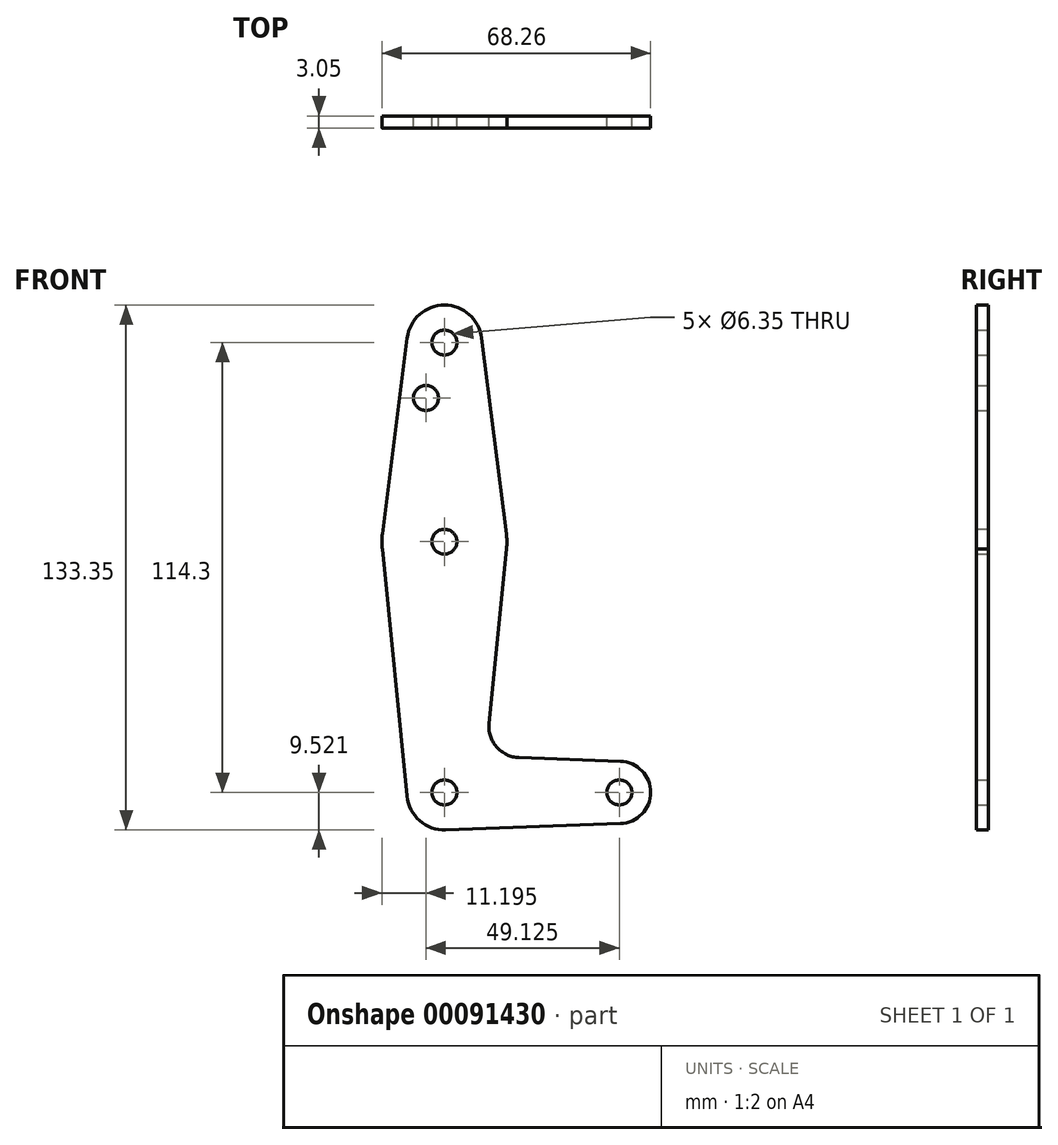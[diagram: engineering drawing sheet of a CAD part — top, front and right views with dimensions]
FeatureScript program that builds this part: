
annotation { "Feature Type Name" : "Feature", "Feature Type Description" : "" }
export const myFeature = defineFeature(function(context is Context, id is Id, definition is map)
    precondition{}
    {
        {
            var Q0;
            Q0=qCreatedBy(makeId("Front.planeOp"),FACE);
            var sketch = newSketch(context, id + "F0", { "sketchPlane" : qUnion([Q0])});
            skLineSegment(sketch, "E0", {"start": v(0, 50.6) * mm, "end": v(0, -63.7) * mm, "construction": true});
            skCircle(sketch, "E1", {"center": v(0, 50.6) * mm, "radius": 9.53 * mm});
            skCircle(sketch, "E2", {"center": v(0, -63.7) * mm, "radius": 9.53 * mm});
            skLineSegment(sketch, "E3", {"start": v(0, -63.7) * mm, "end": v(0, -0.2) * mm, "construction": true});
            skCircle(sketch, "E4", {"center": v(0, 0) * mm, "radius": 15.88 * mm});
            skLineSegment(sketch, "E5", {"start": v(0, -63.7) * mm, "end": v(44.45, -63.7) * mm, "construction": true});
            skCircle(sketch, "E6", {"center": v(44.45, -63.7) * mm, "radius": 7.94 * mm});
            skLineSegment(sketch, "E7", {"start": v(-15.75, 2) * mm, "end": v(-9.45, 51.8) * mm});
            skLineSegment(sketch, "E8", {"start": v(15.75, 2) * mm, "end": v(9.45, 51.8) * mm});
            skLineSegment(sketch, "E9", {"start": v(-15.76, -1.9) * mm, "end": v(-9.48, -64.65) * mm});
            skLineSegment(sketch, "E10", {"start": v(15.76, -1.9) * mm, "end": v(11.33, -46.1) * mm});
            skLineSegment(sketch, "E11", {"start": v(18.96, -54.85) * mm, "end": v(44.73, -55.77) * mm});
            skLineSegment(sketch, "E12", {"start": v(0.34, -73.22) * mm, "end": v(44.73, -71.63) * mm});
            skCircle(sketch, "E13", {"center": v(0, 50.6) * mm, "radius": 3.18 * mm});
            skCircle(sketch, "E14", {"center": v(0, 0) * mm, "radius": 3.18 * mm});
            skCircle(sketch, "E15", {"center": v(0, -63.7) * mm, "radius": 3.18 * mm});
            skCircle(sketch, "E16", {"center": v(44.45, -63.7) * mm, "radius": 3.18 * mm});
            skArc(sketch, "E17.filletArc", {"start": v(11.33, -46.1) * mm, "mid": v(13.26, -52.13) * mm, "end": v(18.96, -54.85) * mm});
            skLineSegment(sketch, "E18", {"start": v(0, 0) * mm, "end": v(0, 36.53) * mm});
            skLineSegment(sketch, "E19", {"start": v(0, 36.53) * mm, "end": v(-4.67, 36.53) * mm});
            skCircle(sketch, "E20", {"center": v(-4.67, 36.53) * mm, "radius": 3.18 * mm});
            skSolve(sketch);
        }
        {
            var Q0;
            {var subQ0=sQuery(id+"F0.wireOp",EDGE,"E7");Q0=makeQuery(id+"F0.imprint","IMPRINT",FACE,{"disambiguationData":[TD([[makeQuery(id+"F0.imprint","IMPRINT",EDGE,{"derivedFrom":subQ0}),-1.0]])]});}
            var Q1;
            Q1=makeQuery(id+"F0.imprint","IMPRINT",FACE,{"disambiguationData":[TD([[makeQuery(id+"F0.imprint","IMPRINT",EDGE,{"derivedFrom":sQuery(id+"F0.wireOp",EDGE,"E13")}),-1.0]])]});
            var Q2;
            Q2=makeQuery(id+"F0.imprint","IMPRINT",FACE,{"disambiguationData":[TD([[makeQuery(id+"F0.imprint","IMPRINT",EDGE,{"derivedFrom":sQuery(id+"F0.wireOp",EDGE,"E14")}),-1.0]])]});
            var Q3;
            {var subQ0=sQuery(id+"F0.wireOp",EDGE,"E9");Q3=makeQuery(id+"F0.imprint","IMPRINT",FACE,{"disambiguationData":[TD([[makeQuery(id+"F0.imprint","IMPRINT",EDGE,{"derivedFrom":subQ0}),1.0]])]});}
            var Q4;
            Q4=makeQuery(id+"F0.imprint","IMPRINT",FACE,{"disambiguationData":[TD([[makeQuery(id+"F0.imprint","IMPRINT",EDGE,{"derivedFrom":sQuery(id+"F0.wireOp",EDGE,"E15")}),-1.0]])]});
            var Q5;
            Q5=makeQuery(id+"F0.imprint","IMPRINT",FACE,{"disambiguationData":[TD([[makeQuery(id+"F0.imprint","IMPRINT",EDGE,{"derivedFrom":sQuery(id+"F0.wireOp",EDGE,"E16")}),-1.0]])]});
            extrude(context, id + "F1", {"entities" : qUnion([Q0, Q1, Q2, Q3, Q4, Q5]), "depth" : 3.05 * mm});
        }
    });
